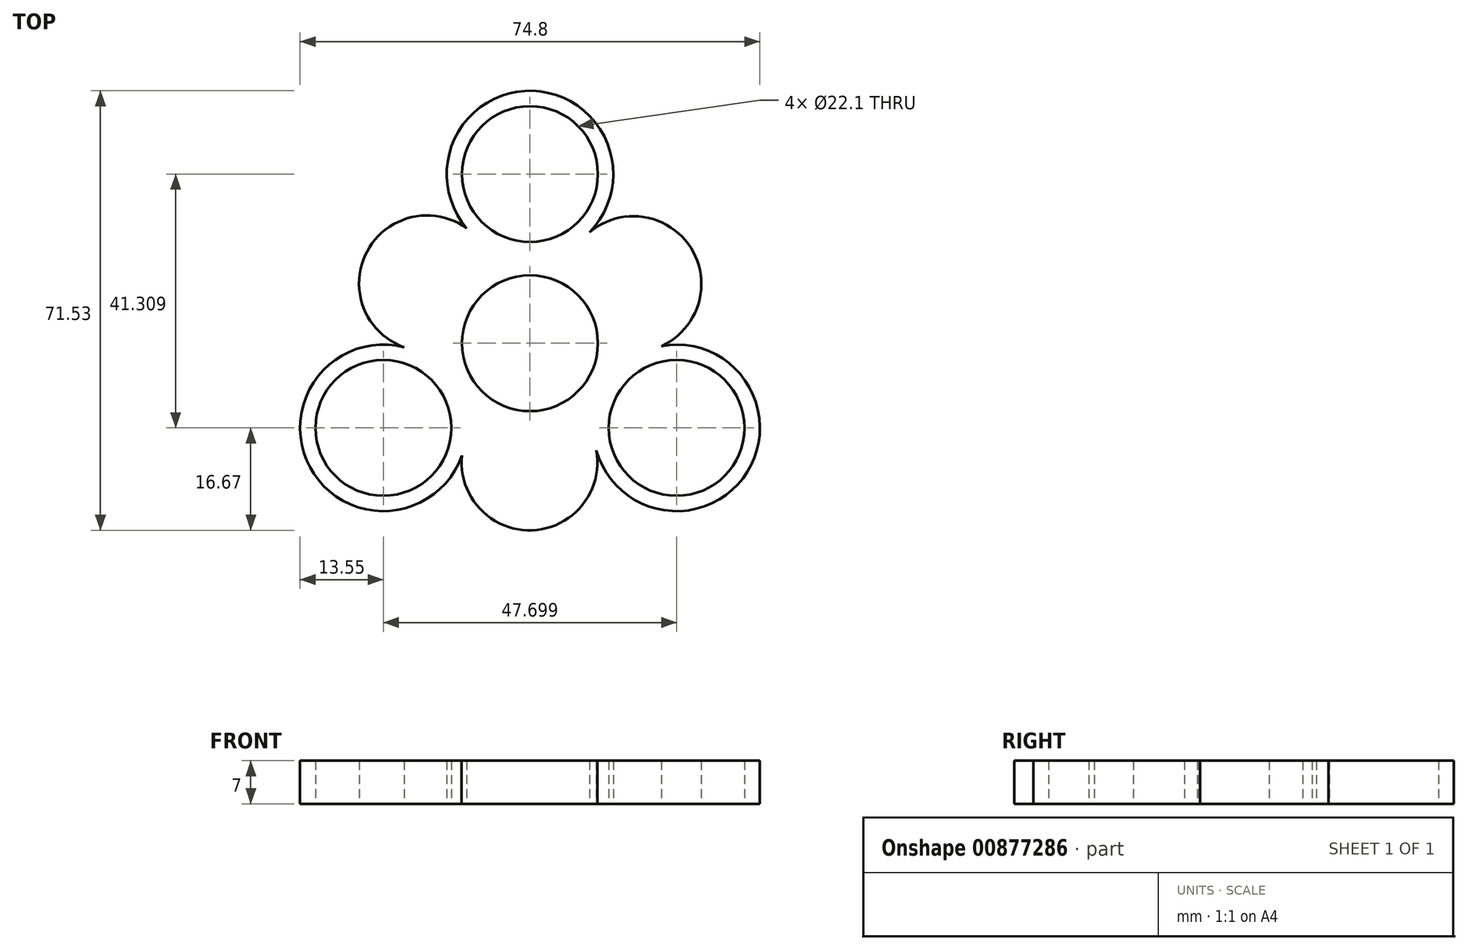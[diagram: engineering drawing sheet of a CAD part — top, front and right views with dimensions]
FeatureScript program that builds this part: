
annotation { "Feature Type Name" : "Feature", "Feature Type Description" : "" }
export const myFeature = defineFeature(function(context is Context, id is Id, definition is map)
    precondition{}
    {
        {
            var Q0;
            Q0=qCreatedBy(makeId("Top.planeOp"),FACE);
            var sketch = newSketch(context, id + "F0", { "sketchPlane" : qUnion([Q0])});
            skCircle(sketch, "E0", {"center": v(0, 0) * mm, "radius": 11.05 * mm});
            skCircle(sketch, "E1", {"center": v(0, 27.54) * mm, "radius": 11.05 * mm});
            skArc(sketch, "E2", {"start": v(9.68, 18.06) * mm, "mid": v(0.44, 41.08) * mm, "end": v(-10.28, 18.71) * mm});
            skArc(sketch, "E3.1.0", {"start": v(-20.48, -0.64) * mm, "mid": v(-35.8, -20.16) * mm, "end": v(-11.07, -18.26) * mm});
            skCircle(sketch, "E3.1.1", {"center": v(-23.85, -13.77) * mm, "radius": 11.05 * mm});
            skArc(sketch, "E3.2.0", {"start": v(10.8, -17.42) * mm, "mid": v(35.36, -20.93) * mm, "end": v(21.35, -0.45) * mm});
            skCircle(sketch, "E3.2.1", {"center": v(23.85, -13.77) * mm, "radius": 11.05 * mm});
            skLineSegment(sketch, "E4", {"start": v(23.85, -13.77) * mm, "end": v(-39.48, 22.93) * mm, "construction": true});
            skArc(sketch, "E5", {"start": v(-10.28, 18.71) * mm, "mid": v(-26.53, 14.9) * mm, "end": v(-20.48, -0.64) * mm});
            skArc(sketch, "E6.1.0", {"start": v(-11.07, -18.26) * mm, "mid": v(0.35, -30.43) * mm, "end": v(10.8, -17.42) * mm});
            skArc(sketch, "E6.2.0", {"start": v(21.35, -0.45) * mm, "mid": v(26.17, 15.52) * mm, "end": v(9.68, 18.06) * mm});
            skSolve(sketch);
        }
        {
            var Q0;
            Q0=makeQuery(id+"F0.imprint","IMPRINT",FACE,{"disambiguationData":[TD([[makeQuery(id+"F0.imprint","IMPRINT",EDGE,{"derivedFrom":sQuery(id+"F0.wireOp",EDGE,"E0")}),-1.0]])]});
            extrude(context, id + "F1", {"entities" : qUnion([Q0]), "depth" : 7 * mm, "offsetDistance" : 25 * mm});
        }
    });
